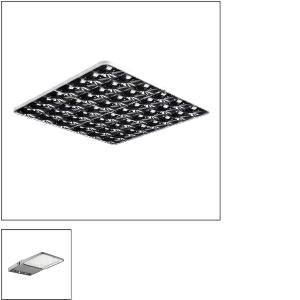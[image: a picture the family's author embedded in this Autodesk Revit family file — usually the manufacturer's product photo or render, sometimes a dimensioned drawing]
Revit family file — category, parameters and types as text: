
# Revit family: siteco_mirrortec_r__indoor___rs05_5nw14093qb_2604
name_source: partatom
category: Lighting Fixtures
units: mm (PartAtom-declared; Revit-internal decimal feet)

## family parameters
Cut with Voids When Loaded = No
Host = Face
Light Source = No
Part Type = Normal
Room Calculation Point = No
Round Connector Dimension = Use Diameter
Shared = No

## types (1)
- 5XA7682G2H2AC (1 x LED, 33820 lm, 305.7 W, 4000K)
    Apparent Load = 306 VA
    CIE Flux Codes = 47 83 98 55 100
    Color Rendering = 70
    Color Temperature = 4000K
    Default Elevation = 1800 mm
    Description = secondary reflector, for Siteco Mirrortec® Indoor, wire hanger, housing, square, of aluminium, coated, metallic grey (RAL 9006), fresnel reflector 100, of PMMA, aluminized, highly specular, light point resolution, fresnel structure, length: 900 mm, width: 900 mm

Light Distribution: RS05
    Height = 12 mm  [stored 0.0393701 ft]
    Lamp = 1 x LED
    Lamp Light Flux = 33820 lm
    Lamp Power = 305.7 W
    Lamp count = 1
    Length = 919 mm
    Luminous efficacy = 111 lm/W
    Manufacturer = Siteco
    ModVariant = No
    Model = 5NW14093QB
    Mounting Place = Ceiling
    Mounting Type = Pendant
    Number of Poles = 1
    OnlyDefault = Yes
    Power Factor = 1
    Product Name = Siteco Mirrortec® Indoor | RS05
    Product group = secondary reflector
    ProductGroupID = 908
    Protection Class = Protection class II
    Protection Degree = IP 66
    RLX_Detail_Level = 1
    RLX_Emergency_Light_Flux = 0 lm
    RLX_Emergency_Type = 0
    RLX_Emergency_Type_DB = No
    RlxData = <blob elided: 103309 chars, md5=0c28db43>
    Socket = socket
    Standby Power = 0 W
    System Light Flux = 33820 lm
    System Power = 306 W
    Type Comments = Floodlight FL 20 midi, floodlight, primary light control with lens, of plastic, primary optical cover: protective disc, of toughened safety glass, transparent, light distribution: RS05, light emission: direct distribution, primary light characteristic: rotationally symmetric, installation type: surface-mounted, LED, High Power LED, rated luminous flux: 38.380lm, luminous efficacy: 126lm/W, light colour: 740, colour temperature: 4000K, control gear: ECG Plus, control: overheat protection, power reduction, digital communication interface, time-dependent luminous flux control, flexible luminous flux parameterisation, electronic power reduction, with terminal, 10-pole, max. 2.5mm², mains connection: 220..240V, AC, 50/60Hz, rated input power: 306W, LED unit, of diecast aluminium, powder-coated, Siteco® metallic grey (DB 702S), corrosivity category C5 mid according to DIN EN ISO 12944, length: 731mm, width: 450mm, height: 76mm, housing frame, of diecast aluminium, powder-coated, Siteco® metallic grey (DB 702S), wall fastening, DALI, protection rating (complete): IP66, insulation class (complete): insulation class II (safety insulation), certification: CE, ENEC, VDE, protection symbol: D, permissible operating ambient temperature: -40..+40°C, permissible operating ambient temperature for outdoor applications: -40..+50°C, standard: DIN EN 12944, packaging unit: 1 piece

individual setting: distance floodlight mirror = 2,5m / reflector tilt = 5°
    Type Image = l_577132_1005944.jpg
    URL = http://relux.com
    VarID = 5xa7682g2h2ac@adj_152965
    Voltage = 0 V
    Weight = 0.00 kg
    Width = 919 mm

note: [stored X ft] marks values corroborated as IEEE doubles in the binary element streams (Revit-internal decimal feet)

## geometry (parser evidence)
native form markers: Blend x4, Sweep x10
no freeform markers — native parametric forms only
